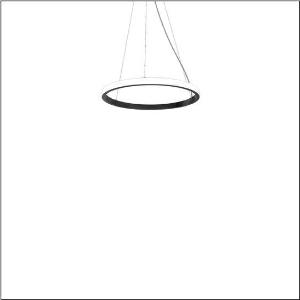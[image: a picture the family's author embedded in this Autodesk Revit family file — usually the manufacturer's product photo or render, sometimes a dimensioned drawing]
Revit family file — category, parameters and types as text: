
# Revit family: silica_r__21_ring-o_5pjbo1d1104a_1dcd
name_source: partatom
category: Lighting Fixtures
units: mm (PartAtom-declared; Revit-internal decimal feet)

## family parameters
Cut with Voids When Loaded = No
Host = Face
Light Source = No
Part Type = Normal
Room Calculation Point = No
Round Connector Dimension = Use Diameter
Shared = No

## types (1)
- Silica® 21 Ring-O (1 x LED, 3740 lm, 60 W, 3000K)
    Apparent Load = 60 VA
    CIE Flux Codes = 2 16 49 50 100
    Color Rendering = 80
    Color Temperature = 3000K
    Default Elevation = 1800 mm
    Description = Silica® 21 Ring-O, suspended luminaire, of PMMA, frosted, light emission: outer ring side luminous distribution, primary light characteristic: symmetric, installation type: suspended mounting, LED, rated luminous flux: 3.744lm, luminous efficacy: 62lm/W, light colour: 830, colour temperature: 3000K, with terminal, 5-pole, mains connection: 230V, AC/DC, 0/50..60Hz, rated input power: 60W, housing, of extruded aluminium section, jet black (RAL 9005), diameter: 610mm, ceiling canopy, jet black (RAL 9005), protection rating (lamp compartment): IP40, insulation class (complete): insulation class I (protective earthing), certification: CE, impact resistance: IK02, permissible operating ambient temperature: 0..+35°C, packaging unit: 1 piece
    Height = 48 mm  [stored 0.15748 ft]
    Lamp = 1 x LED
    Lamp Light Flux = 3740 lm
    Lamp Power = 60 W
    Lamp count = 1
    Length = 610 mm
    Luminous efficacy = 62 lm/W
    Manufacturer = Siteco
    ModVariant = No
    Model = 5PJBO1D1104A
    Mounting Place = Ceiling
    Mounting Type = Pendant
    Number of Poles = 1
    OnlyDefault = Yes
    Power Factor = 1
    Product Name = Silica® 21 Ring-O
    Product group = suspended luminaire
    ProductGroupID = 904
    Protection Class = Protection class I
    Protection Degree = IP 40
    RLX_Detail_Level = 1
    RLX_Emergency_Light_Flux = 0 lm
    RLX_Emergency_Type = 0
    RLX_Emergency_Type_DB = No
    RlxData = <blob elided: 12137 chars, md5=712e4ecb>
    Socket = socket
    Standby Power = 0 W
    System Light Flux = 3740 lm
    System Power = 60 W
    Type Comments = Product without accessories
    Type Image = l_1258377.jpg
    URL = http://relux.com
    VarID = ---
    Voltage = 0 V
    Weight = 0.00 kg
    Width = 0 mm  [stored 0 ft]

note: [stored X ft] marks values corroborated as IEEE doubles in the binary element streams (Revit-internal decimal feet)

## geometry (parser evidence)
native form markers: Sweep x14
no freeform markers — native parametric forms only
